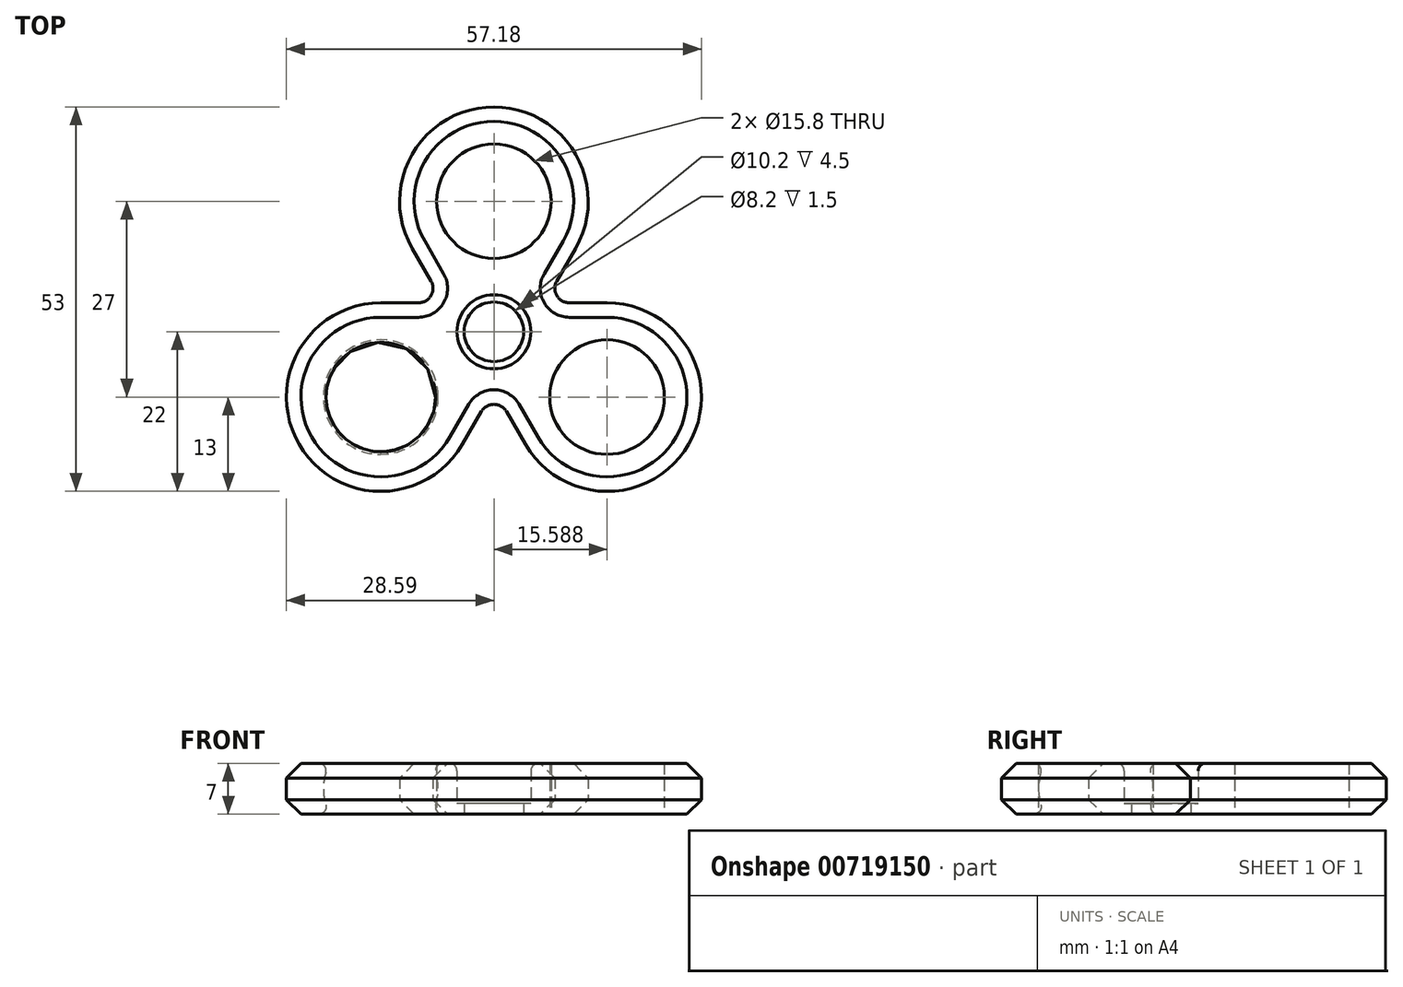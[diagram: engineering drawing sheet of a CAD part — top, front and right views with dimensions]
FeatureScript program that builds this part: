
annotation { "Feature Type Name" : "Feature", "Feature Type Description" : "" }
export const myFeature = defineFeature(function(context is Context, id is Id, definition is map)
    precondition{}
    {
        {
            var Q0;
            Q0=qCreatedBy(makeId("Top.planeOp"),FACE);
            var sketch = newSketch(context, id + "F0", { "sketchPlane" : qUnion([Q0])});
            skLineSegment(sketch, "E0", {"start": v(0, 0) * mm, "end": v(0, 18) * mm, "construction": true});
            skCircle(sketch, "E1", {"center": v(0, 18) * mm, "radius": 7.9 * mm});
            skArc(sketch, "E2", {"start": v(11.26, 11.5) * mm, "mid": v(0, 31) * mm, "end": v(-11.26, 11.5) * mm});
            skCircle(sketch, "E3", {"center": v(0, 0) * mm, "radius": 5.1 * mm});
            skArc(sketch, "E4.1.2", {"start": v(-15.59, 4) * mm, "mid": v(-26.85, -15.5) * mm, "end": v(-4.33, -15.5) * mm});
            skCircle(sketch, "E4.1.3", {"center": v(-15.59, -9) * mm, "radius": 7.9 * mm});
            skArc(sketch, "E4.2.2", {"start": v(4.33, -15.5) * mm, "mid": v(26.85, -15.5) * mm, "end": v(15.59, 4) * mm});
            skCircle(sketch, "E4.2.3", {"center": v(15.59, -9) * mm, "radius": 7.9 * mm});
            skLineSegment(sketch, "E5", {"start": v(0, 0) * mm, "end": v(-15.59, -9) * mm, "construction": true});
            skLineSegment(sketch, "E6", {"start": v(0, 0) * mm, "end": v(15.59, -9) * mm, "construction": true});
            skCircle(sketch, "E7", {"center": v(0, 0) * mm, "radius": 8 * mm, "construction": true});
            skLineSegment(sketch, "E8", {"start": v(-15.59, 4) * mm, "end": v(-6.93, 4) * mm});
            skLineSegment(sketch, "E9.MirrorCS", {"start": v(-4.33, -15.5) * mm, "end": v(0, -8) * mm});
            skLineSegment(sketch, "E10.1.0", {"start": v(4.33, -15.5) * mm, "end": v(0, -8) * mm});
            skLineSegment(sketch, "E10.1.1", {"start": v(15.59, 4) * mm, "end": v(6.93, 4) * mm});
            skLineSegment(sketch, "E10.2.0", {"start": v(11.26, 11.5) * mm, "end": v(6.93, 4) * mm});
            skLineSegment(sketch, "E10.2.1", {"start": v(-11.26, 11.5) * mm, "end": v(-6.93, 4) * mm});
            skSolve(sketch);
        }
        {
            var Q0;
            Q0=qSketchRegion(id+"F0",true);
            extrude(context, id + "F1", {"entities" : qUnion([Q0]), "depth" : 7 * mm, "offsetDistance" : 25 * mm});
        }
        {
            var Q0;
            Q0=makeQuery(id+"F1.opExtrude","SWEPT_EDGE",EDGE,{"disambiguationData":[OSD([sQuery(id+"F0.wireOp",EDGE,"hYaDFHxH-SQ1h-cJ0F-NxPf-ypNw5k6PqgM9"),sQuery(id+"F0.wireOp",EDGE,"E4.1.2")])]});
            var Q1;
            Q1=makeQuery(id+"F1.opExtrude","SWEPT_EDGE",EDGE,{"disambiguationData":[OSD([sQuery(id+"F0.wireOp",EDGE,"hYaDFHxH-SQ1h-cJ0F-NxPf-ypNw5k6PqgM9"),sQuery(id+"F0.wireOp",EDGE,"E4.2.2")])]});
            var Q2;
            Q2=makeQuery(id+"F1.opExtrude","SWEPT_EDGE",EDGE,{"disambiguationData":[OSD([sQuery(id+"F0.wireOp",EDGE,"E4.2.2"),sQuery(id+"F0.wireOp",EDGE,"79da703c-30cb-4167-bd47-66bc16433dd5.trimOffspring")])]});
            var Q3;
            Q3=makeQuery(id+"F1.opExtrude","SWEPT_EDGE",EDGE,{"disambiguationData":[OSD([sQuery(id+"F0.wireOp",EDGE,"E2"),sQuery(id+"F0.wireOp",EDGE,"79da703c-30cb-4167-bd47-66bc16433dd5.trimOffspring")])]});
            var Q4;
            Q4=makeQuery(id+"F1.opExtrude","SWEPT_EDGE",EDGE,{"disambiguationData":[OSD([sQuery(id+"F0.wireOp",EDGE,"E2"),sQuery(id+"F0.wireOp",EDGE,"007a9c35-0cf0-4482-a21c-6fcd3d696d74.trimOffspring")])]});
            var Q5;
            Q5=makeQuery(id+"F1.opExtrude","SWEPT_EDGE",EDGE,{"disambiguationData":[OSD([sQuery(id+"F0.wireOp",EDGE,"E4.1.2"),sQuery(id+"F0.wireOp",EDGE,"007a9c35-0cf0-4482-a21c-6fcd3d696d74.trimOffspring")])]});
            var Q6;
            Q6=makeQuery(id+"F1.opExtrude","SWEPT_EDGE",EDGE,{"disambiguationData":[OSD([sQuery(id+"F0.wireOp",EDGE,"E9.MirrorCS"),sQuery(id+"F0.wireOp",EDGE,"E10.1.0")])]});
            var Q7;
            Q7=makeQuery(id+"F1.opExtrude","SWEPT_EDGE",EDGE,{"disambiguationData":[OSD([sQuery(id+"F0.wireOp",EDGE,"E10.1.1"),sQuery(id+"F0.wireOp",EDGE,"E10.2.0")])]});
            var Q8;
            Q8=makeQuery(id+"F1.opExtrude","SWEPT_EDGE",EDGE,{"disambiguationData":[OSD([sQuery(id+"F0.wireOp",EDGE,"E8"),sQuery(id+"F0.wireOp",EDGE,"E10.2.1")])]});
            fillet(context, id + "F2", {"entities" : qUnion([Q0, Q1, Q2, Q3, Q4, Q5, Q6, Q7, Q8]), "radius" : 2 * mm, "tangentPropagation" : true, "allowEdgeOverflow" : false});
        }
        {
            var Q0;
            Q0=makeQuery(id+"F1.opExtrude","CAP_EDGE",EDGE,{"disambiguationData":[OSD([sQuery(id+"F0.wireOp",EDGE,"E4.2.2")])],"isStart":true});
            var Q1;
            Q1=makeQuery(id+"F1.opExtrude","CAP_EDGE",EDGE,{"disambiguationData":[OSD([sQuery(id+"F0.wireOp",EDGE,"E4.2.2")])],"isStart":false});
            chamfer(context, id + "F3", {"entities" : qUnion([Q0, Q1]), "width" : 2 * mm, "tangentPropagation" : true});
        }
        {
            var Q0;
            Q0=qCreatedBy(makeId("Top.planeOp"),FACE);
            var sketch = newSketch(context, id + "F4", { "sketchPlane" : qUnion([Q0])});
            skCircle(sketch, "E11.0", {"center": v(-15.59, -9) * mm, "radius": 7.9 * mm, "construction": true});
            skLineSegment(sketch, "E12", {"start": v(0, 0) * mm, "end": v(-15.59, -9) * mm, "construction": true});
            skCircle(sketch, "E13.0", {"center": v(0, 18) * mm, "radius": 7.9 * mm, "construction": true});
            skLineSegment(sketch, "E14", {"start": v(0, 0) * mm, "end": v(0, 18) * mm, "construction": true});
            skCircle(sketch, "E15.0", {"center": v(15.59, -9) * mm, "radius": 7.9 * mm, "construction": true});
            skLineSegment(sketch, "E16", {"start": v(0, 0) * mm, "end": v(15.59, -9) * mm, "construction": true});
            skSolve(sketch);
        }
        {
            var Q0;
            {var subQ0=sQuery(id+"F0.wireOp",EDGE,"E4.1.2");Q0=makeQuery(id+"F3.opChamfer","BLEND_EDGE",EDGE,{"blendedFrom":[makeQuery(id+"F1.opExtrude","CAP_EDGE",EDGE,{"disambiguationData":[OSD([subQ0])],"isStart":false}),makeQuery(id+"F1.opExtrude","CAP_FACE",FACE,{"disambiguationData":[OSD([sQuery(id+"F0.wireOp",EDGE,"E1"),sQuery(id+"F0.wireOp",EDGE,"E2"),sQuery(id+"F0.wireOp",EDGE,"E3"),sQuery(id+"F0.wireOp",EDGE,"hYaDFHxH-SQ1h-cJ0F-NxPf-ypNw5k6PqgM9"),subQ0,sQuery(id+"F0.wireOp",EDGE,"E4.1.3"),sQuery(id+"F0.wireOp",EDGE,"E4.2.2"),sQuery(id+"F0.wireOp",EDGE,"E4.2.3"),sQuery(id+"F0.wireOp",EDGE,"79da703c-30cb-4167-bd47-66bc16433dd5.trimOffspring"),sQuery(id+"F0.wireOp",EDGE,"007a9c35-0cf0-4482-a21c-6fcd3d696d74.trimOffspring")])],"isStart":false})],"blendedInto":[makeQuery(id+"F1.opExtrude","CAP_FACE",FACE,{"disambiguationData":[OSD([sQuery(id+"F0.wireOp",EDGE,"E1"),sQuery(id+"F0.wireOp",EDGE,"E2"),sQuery(id+"F0.wireOp",EDGE,"E3"),sQuery(id+"F0.wireOp",EDGE,"hYaDFHxH-SQ1h-cJ0F-NxPf-ypNw5k6PqgM9"),subQ0,sQuery(id+"F0.wireOp",EDGE,"E4.1.3"),sQuery(id+"F0.wireOp",EDGE,"E4.2.2"),sQuery(id+"F0.wireOp",EDGE,"E4.2.3"),sQuery(id+"F0.wireOp",EDGE,"79da703c-30cb-4167-bd47-66bc16433dd5.trimOffspring"),sQuery(id+"F0.wireOp",EDGE,"007a9c35-0cf0-4482-a21c-6fcd3d696d74.trimOffspring")])],"isStart":false})]});}
            cPoint(context, id + "F5", {"entities" : qUnion([Q0]), "parameter" : 0.5});
        }
        {
            var Q0;
            Q0=sQuery(id+"F4.wireOp",VERTEX,"E12.start");
            var Q1;
            Q1=sQuery(id+"F4.wireOp",VERTEX,"E11.0.center");
            var Q2;
            Q2 = qCreatedBy(id + "F5" ,VERTEX);
            cPlane(context, id + "F6", {"entities" : qUnion([Q0, Q1, Q2]), "cplaneType" : CPlaneType.THREE_POINT, "offset" : 25 * mm, "width" : 150 * mm, "height" : 150 * mm});
        }
        {
            var Q0;
            Q0=qCreatedBy(id+"F6.planeOp",FACE);
            var sketch = newSketch(context, id + "F7", { "sketchPlane" : qUnion([Q0])});
            skLineSegment(sketch, "E17.0", {"start": v(-25.9, 7) * mm, "end": v(-25.08, 7) * mm, "construction": true});
            skLineSegment(sketch, "E18.1", {"start": v(-25.9, 0) * mm, "end": v(-25.08, 0) * mm, "construction": true});
            skLineSegment(sketch, "E19", {"start": v(-25.9, 7) * mm, "end": v(-25.9, 0) * mm});
            skLineSegment(sketch, "E20", {"start": v(-18, 0) * mm, "end": v(-18, 7) * mm, "construction": true});
            skArc(sketch, "E21", {"start": v(-25.08, 7) * mm, "mid": v(-25.9, 3.5) * mm, "end": v(-25.08, 0) * mm});
            skLineSegment(sketch, "E22", {"start": v(-25.9, 7) * mm, "end": v(-25.08, 7) * mm});
            skLineSegment(sketch, "E23", {"start": v(-25.9, 0) * mm, "end": v(-25.08, 0) * mm});
            skLineSegment(sketch, "E24.trimOffspring", {"start": v(-18, 7) * mm, "end": v(-10.1, 7) * mm, "construction": true});
            skLineSegment(sketch, "E25.trimOffspring", {"start": v(-18, 0) * mm, "end": v(-10.1, 0) * mm, "construction": true});
            skSolve(sketch);
        }
        {
            var Q0;
            Q0 = qSketchRegion(id + "F7", true);
            var Q1;
            Q1=sQuery(id+"F7.wireOp",EDGE,"E20");
            revolve(context, id + "F8", {"operationType" : NewBodyOperationType.ADD, "surfaceOperationType" : NewSurfaceOperationType.NEW, "entities" : qUnion([Q0]), "axis" : qUnion([Q1]), "revolveType" : RevolveType.FULL});
        }
        {
            var Q0;
            Q0=makeQuery(id+"F8.opRevolve","SWEPT_EDGE",EDGE,{"disambiguationData":[OSD([sQuery(id+"F7.wireOp",EDGE,"E21"),sQuery(id+"F7.wireOp",EDGE,"E22")])]});
            var Q1;
            Q1=makeQuery(id+"F8.opRevolve","SWEPT_EDGE",EDGE,{"disambiguationData":[OSD([sQuery(id+"F7.wireOp",EDGE,"E21"),sQuery(id+"F7.wireOp",EDGE,"E23")])]});
            var Q2;
            Q2=makeQuery(id+"Fynh9oEJvHPlE7w_1.2.F8.opRevolve","SWEPT_EDGE",EDGE,{"disambiguationData":[OSD([sQuery(id+"F7.wireOp",EDGE,"E21"),sQuery(id+"F7.wireOp",EDGE,"E22")])]});
            var Q3;
            Q3=makeQuery(id+"Fynh9oEJvHPlE7w_1.2.F8.opRevolve","SWEPT_EDGE",EDGE,{"disambiguationData":[OSD([sQuery(id+"F7.wireOp",EDGE,"E21"),sQuery(id+"F7.wireOp",EDGE,"E23")])]});
            var Q4;
            Q4=makeQuery(id+"Fynh9oEJvHPlE7w_1.1.F8.opRevolve","SWEPT_EDGE",EDGE,{"disambiguationData":[OSD([sQuery(id+"F7.wireOp",EDGE,"E21"),sQuery(id+"F7.wireOp",EDGE,"E22")])]});
            var Q5;
            Q5=makeQuery(id+"Fynh9oEJvHPlE7w_1.1.F8.opRevolve","SWEPT_EDGE",EDGE,{"disambiguationData":[OSD([sQuery(id+"F7.wireOp",EDGE,"E21"),sQuery(id+"F7.wireOp",EDGE,"E23")])]});
            var Q6;
            Q6=makeQuery(id+"F1.opExtrude","CAP_EDGE",EDGE,{"disambiguationData":[OSD([sQuery(id+"F0.wireOp",EDGE,"E3")])],"isStart":false});
            fillet(context, id + "F9", {"entities" : qUnion([Q0, Q1, Q2, Q3, Q4, Q5, Q6]), "radius" : 1 * mm, "tangentPropagation" : true, "allowEdgeOverflow" : false});
        }
        {
            var Q0;
            Q0=qCreatedBy(makeId("Top.planeOp"),FACE);
            var sketch = newSketch(context, id + "F10", { "sketchPlane" : qUnion([Q0])});
            skCircle(sketch, "E26.0", {"center": v(0, 0) * mm, "radius": 5.1 * mm});
            skCircle(sketch, "E27", {"center": v(0, 0) * mm, "radius": 4.1 * mm});
            skSolve(sketch);
        }
        {
            var Q0;
            Q0 = qSketchRegion(id + "F10", true);
            extrude(context, id + "F11", {"entities" : qUnion([Q0]), "operationType" : NewBodyOperationType.ADD, "depth" : 1.5 * mm, "offsetDistance" : 25 * mm});
        }
    });
